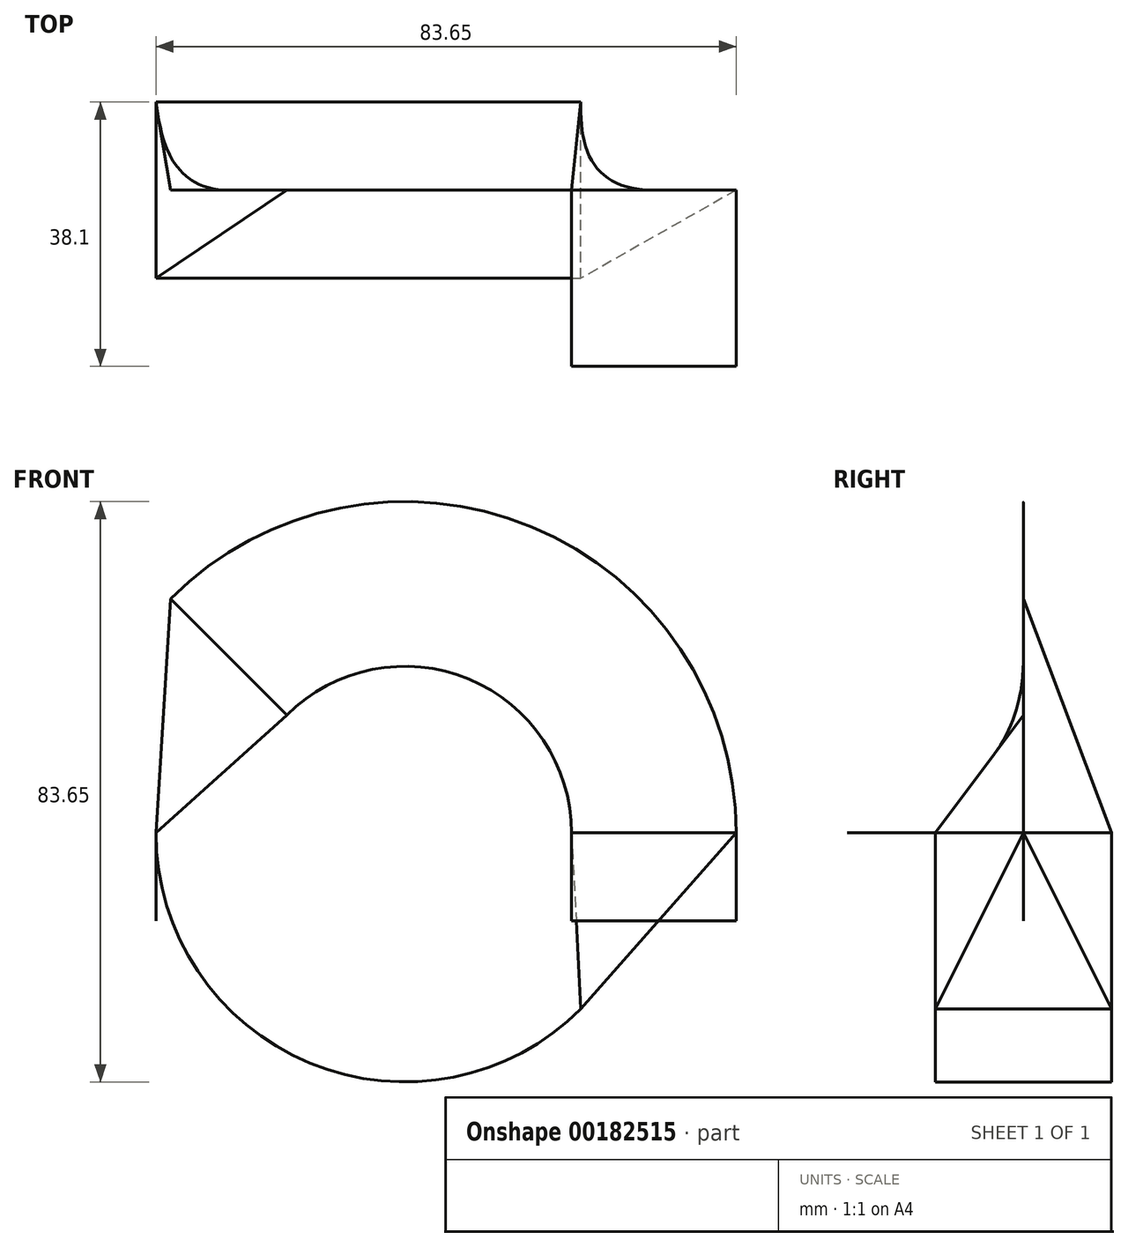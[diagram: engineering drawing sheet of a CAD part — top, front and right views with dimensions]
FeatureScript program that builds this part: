
annotation { "Feature Type Name" : "Feature", "Feature Type Description" : "" }
export const myFeature = defineFeature(function(context is Context, id is Id, definition is map)
    precondition{}
    {
        {
            var Q0;
            Q0=qCreatedBy(makeId("Front.planeOp"),FACE);
            var sketch = newSketch(context, id + "F0", { "sketchPlane" : qUnion([Q0])});
            skArc(sketch, "E0", {"start": v(-35.89, 0) * mm, "mid": v(0, 35.89) * mm, "end": v(35.89, 0) * mm, "construction": true});
            skArc(sketch, "E1", {"start": v(-35.89, 0) * mm, "mid": v(0, -35.89) * mm, "end": v(35.89, 0) * mm, "construction": true});
            skLineSegment(sketch, "E2", {"start": v(24.02, 0) * mm, "end": v(35.89, 0) * mm});
            skLineSegment(sketch, "E3", {"start": v(35.89, 0) * mm, "end": v(47.76, 0) * mm});
            skArc(sketch, "E4", {"start": v(-35.89, 0) * mm, "mid": v(0, 35.89) * mm, "end": v(35.89, 0) * mm});
            skArc(sketch, "E5", {"start": v(-35.89, 0) * mm, "mid": v(0, -35.89) * mm, "end": v(35.89, 0) * mm});
            skSolve(sketch);
        }
        {
            var Q0;
            Q0=sQuery(id+"F0.wireOp",EDGE,"E3");
            var Q1;
            Q1=sQuery(id+"F0.wireOp",EDGE,"E2");
            extrude(context, id + "F1", {"bodyType" : ToolBodyType.SURFACE, "surfaceEntities" : qUnion([Q0, Q1]), "depth" : 25.4 * mm});
        }
        {
            var Q0;
            Q0=makeQuery(id+"F1.opExtrude","SWEPT_FACE",FACE,{"disambiguationData":[OSD([sQuery(id+"F0.wireOp",EDGE,"E2"),sQuery(id+"F0.wireOp",EDGE,"E3")])]});
            var sketch = newSketch(context, id + "F2", { "sketchPlane" : qUnion([Q0])});
            skLineSegment(sketch, "E6.0.0", {"start": v(47.76, 25.4) * mm, "end": v(24.02, 25.4) * mm});
            skLineSegment(sketch, "E6.0.1", {"start": v(24.02, 25.4) * mm, "end": v(24.02, 0) * mm});
            skLineSegment(sketch, "E6.0.2", {"start": v(24.02, 0) * mm, "end": v(47.76, 0) * mm});
            skLineSegment(sketch, "E6.0.3", {"start": v(47.76, 0) * mm, "end": v(47.76, 25.4) * mm});
            skPoint(sketch, "E7.0", {"position": v(-35.89, 0) * mm});
            skPoint(sketch, "E8", {"position": v(24.02, 12.7) * mm});
            skLineSegment(sketch, "E9.0", {"start": v(-35.89, 0) * mm, "end": v(35.89, 0) * mm});
            skPoint(sketch, "E10.MirrorP", {"position": v(24.02, -12.7) * mm});
            skLineSegment(sketch, "E11", {"start": v(-35.89, 12.7) * mm, "end": v(-35.89, -12.7) * mm});
            skSolve(sketch);
        }
        {
            var Q0;
            Q0=sQuery(id+"F2.wireOp",EDGE,"E6.0.2");
            extrude(context, id + "F3", {"bodyType" : ToolBodyType.SURFACE, "surfaceEntities" : qUnion([Q0]), "depth" : 12.7 * mm});
        }
        {
            var Q0;
            Q0=sQuery(id+"F2.wireOp",EDGE,"E11");
            extrude(context, id + "F4", {"bodyType" : ToolBodyType.SURFACE, "surfaceEntities" : qUnion([Q0]), "depth" : 12.7 * mm});
        }
        {
            var Q0;
            Q0=qCreatedBy(makeId("Right.planeOp"),FACE);
            var sketch = newSketch(context, id + "F5", { "sketchPlane" : qUnion([Q0])});
            skLineSegment(sketch, "E12", {"start": v(0, 0) * mm, "end": v(-111.65, 0) * mm, "construction": true});
            skSolve(sketch);
        }
        {
            var Q0;
            Q0=sQuery(id+"F2.wireOp",EDGE,"E6.0.2");
            var Q1;
            Q1=sQuery(id+"F5.wireOp",EDGE,"E12");
            revolve(context, id + "F6", {"bodyType" : ToolBodyType.SURFACE, "surfaceEntities" : qUnion([Q0]), "axis" : qUnion([Q1]), "revolveType" : RevolveType.ONE_DIRECTION, "angle" : 135 * degree});
        }
        {
            var Q0;
            Q0=makeQuery(id+"F6.opRevolve","CAP_EDGE",EDGE,{"disambiguationData":[OSD([sQuery(id+"F2.wireOp",EDGE,"E6.0.2")])],"isStart":false});
            var Q1;
            Q1=sQuery(id+"F2.wireOp",EDGE,"E11");
            loft(context, id + "F7", {"bodyType" : ToolBodyType.SURFACE, "wireProfilesArray" : [{ "wireProfileEntities" : qUnion([Q0]) }, { "wireProfileEntities" : qUnion([Q1]) }]});
        }
        {
            var Q0;
            Q0=makeQuery(id+"F7.opLoft","MID_CAP_EDGE",EDGE,{"disambiguationData":[OSD([sQuery(id+"F2.wireOp",VERTEX,"E11.start"),sQuery(id+"F2.wireOp",VERTEX,"E11.end"),sQuery(id+"F2.wireOp",EDGE,"E11")])],"capPos":1.0});
            var Q1;
            Q1=sQuery(id+"F5.wireOp",EDGE,"E12");
            revolve(context, id + "F8", {"bodyType" : ToolBodyType.SURFACE, "surfaceEntities" : qUnion([Q0]), "axis" : qUnion([Q1]), "revolveType" : RevolveType.ONE_DIRECTION, "angle" : 135 * degree});
        }
        {
            var Q0;
            Q0=makeQuery(id+"F6.opRevolve","CAP_EDGE",EDGE,{"disambiguationData":[OSD([sQuery(id+"F2.wireOp",EDGE,"E6.0.2")])],"isStart":true});
            var Q1;
            Q1=makeQuery(id+"F8.opRevolve","CAP_EDGE",EDGE,{"disambiguationData":[OSD([sQuery(id+"F2.wireOp",VERTEX,"E11.start"),sQuery(id+"F2.wireOp",VERTEX,"E11.end"),sQuery(id+"F2.wireOp",EDGE,"E11")])],"isStart":false});
            var Q2;
            Q2=makeQuery(id+"F6.opRevolve","CAP_VERTEX",VERTEX,{"disambiguationData":[OSD([sQuery(id+"F2.wireOp",VERTEX,"E6.0.2.start")])],"isStart":true});
            var Q3;
            Q3=makeQuery(id+"F8.opRevolve","CAP_VERTEX",VERTEX,{"disambiguationData":[OSD([sQuery(id+"F2.wireOp",VERTEX,"E11.end")])],"isStart":false});
            loft(context, id + "F9", {"bodyType" : ToolBodyType.SURFACE, "wireProfilesArray" : [{ "wireProfileEntities" : qUnion([Q0]) }, { "wireProfileEntities" : qUnion([Q1]) }], "matchConnections" : true, "connections" : [{ "connectionEntities" : qUnion([Q2, Q3]), "connectionEdgeQueries" : qUnion([]), "connectionEdgeParameters" : [] }]});
        }
    });
